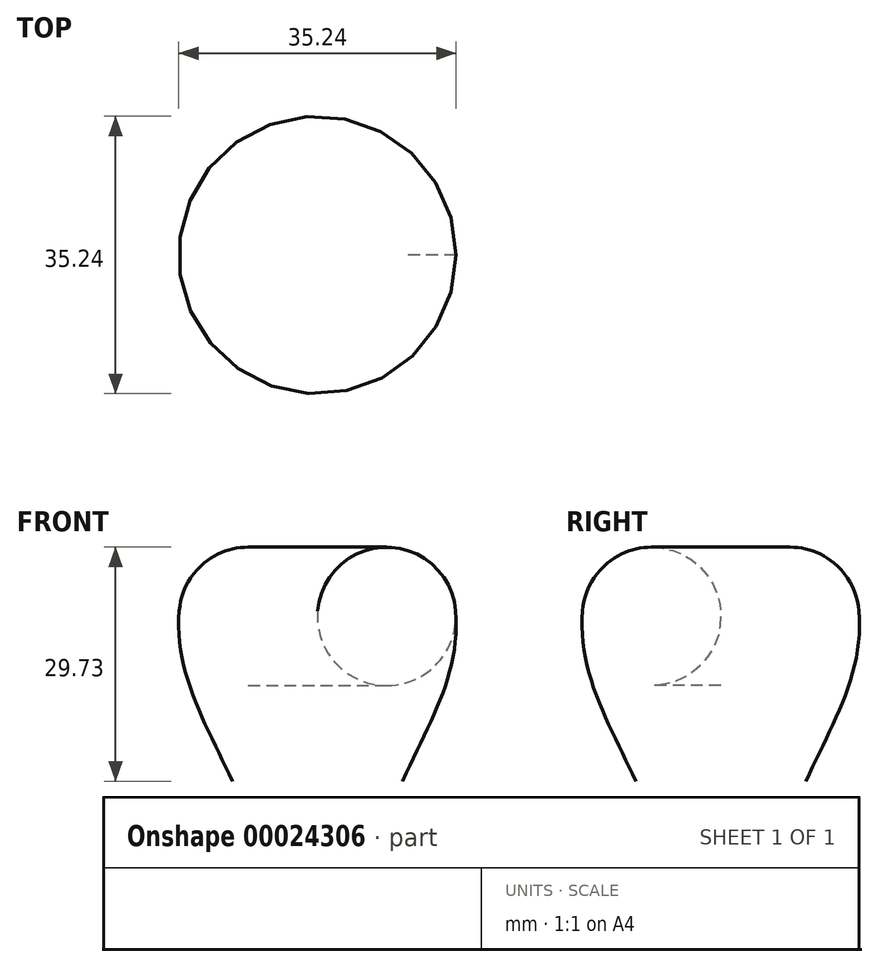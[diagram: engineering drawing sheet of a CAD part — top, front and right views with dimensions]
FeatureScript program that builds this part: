
annotation { "Feature Type Name" : "Feature", "Feature Type Description" : "" }
export const myFeature = defineFeature(function(context is Context, id is Id, definition is map)
    precondition{}
    {
        {
            var Q0;
            Q0=qCreatedBy(makeId("Right.planeOp"),FACE);
            var sketch = newSketch(context, id + "F0", { "sketchPlane" : qUnion([Q0])});
            skLineSegment(sketch, "E0", {"start": v(0, 33.02) * mm, "end": v(0, 0) * mm, "construction": true});
            skArc(sketch, "E1", {"start": v(17.55, 24.94) * mm, "mid": v(8.43, 33.01) * mm, "end": v(0, 24.23) * mm});
            skPoint(sketch, "E2", {"position": v(0, 16.51) * mm});
            skLineSegment(sketch, "E3", {"start": v(0, 16.51) * mm, "end": v(16.51, 16.51) * mm, "construction": true});
            skArc(sketch, "E4", {"start": v(0, 5.66) * mm, "mid": v(4.45, 0.13) * mm, "end": v(10.8, 3.3) * mm});
            skLineSegment(sketch, "E5", {"start": v(0, 33.02) * mm, "end": v(21.6, 33.02) * mm, "construction": true});
            skLineSegment(sketch, "E6", {"start": v(0, 24.23) * mm, "end": v(0, 5.66) * mm});
            skFitSpline(sketch, "E7", {"points": [v(17.55, 24.94) * mm, v(10.8, 3.3) * mm], "startDerivative": vector(1.92, -23.68) * mm, "endDerivative": vector(-10.68, -23.17) * mm});
            skSolve(sketch);
        }
        {
            var Q0;
            Q0=makeQuery(id+"F0.imprint","IMPRINT",FACE,{"disambiguationData":[TD([[makeQuery(id+"F0.imprint","IMPRINT",EDGE,{"derivedFrom":sQuery(id+"F0.wireOp",EDGE,"E1")}),1.0]])]});
            var Q1;
            Q1=sQuery(id+"F0.wireOp",EDGE,"E6");
            revolve(context, id + "F1", {"entities" : qUnion([Q0]), "axis" : qUnion([Q1]), "revolveType" : RevolveType.FULL});
        }
    });
